# Revit family: Sanitary_Showers_AXOR_36724CHN-AXOR-Citterio-E-Porter-unit-120_NEW
name_source: partatom
category: Plumbing Fixtures
revit_build: Autodesk Revit 2018 (Build: 20170223_1515(x64)
units: mm (PartAtom-declared; Revit-internal decimal feet)

## family parameters
Always vertical = No
Cut with Voids When Loaded = No
OmniClass Number = 23.31.17.00
OmniClass Title = Showers
Part Type = Normal
Room Calculation Point = No
Round Connector Dimension = Use Diameter
Shared = No
Work Plane-Based = Yes

## types (4) — shared parameters
Always visible = Yes
BIMobject category = Showers
Connector Description = Water Inlet 12.7mm
Default Elevation = 1219.2 mm  [stored 4 ft]
Description = AXOR Citterio E Porter unit 120/120 softsquare
Design country = Germany
Diameter = 13 mm
EAN code = 4059625427071
Edition number = 1
IFC Classification = Sanitary Terminal
Manufacturer = AXOR
Manufacturer country = Germany
Manufacturer name = AXOR
Material 2 = AXOR - Plastic - Gray
Material main = Metal
Material secondary = Chrome
Model = 36724CHN
OmniClass Code = 23-31 17 00
OmniClass Description = Showers
Product Guid = 57db118a-c591-40d2-a82b-5c2f5085a4e2
Product SKU = 36724CHN
Product data url = https://bimobject.com
Product family = AXOR Citterio E
Product group = Wall outlet
Product name = 36724CHN AXOR Citterio E Porter unit 120/120 softsquare
QR code = https://bimobject.com
URL = https://www.axor-design.com
Weight Net (Kg) = 1

## per-type parameters (varying)
| type | Material 1 |
| 007 Chrome | AXOR - Metal - 007 Chrome |
| 347 Brushed Black Chrome | AXOR - Metal - 347 Brushed Black Chrome |
| 677 Matt Black | AXOR - Metal - 677 Matt Black |
| 997 Polished Gold Optic | AXOR - Metal - 997 Polished Gold Optic |

note: [stored X ft] marks values corroborated as IEEE doubles in the binary element streams (Revit-internal decimal feet)

## geometry (parser evidence)
native form markers: Sweep x2
no freeform markers — native parametric forms only
